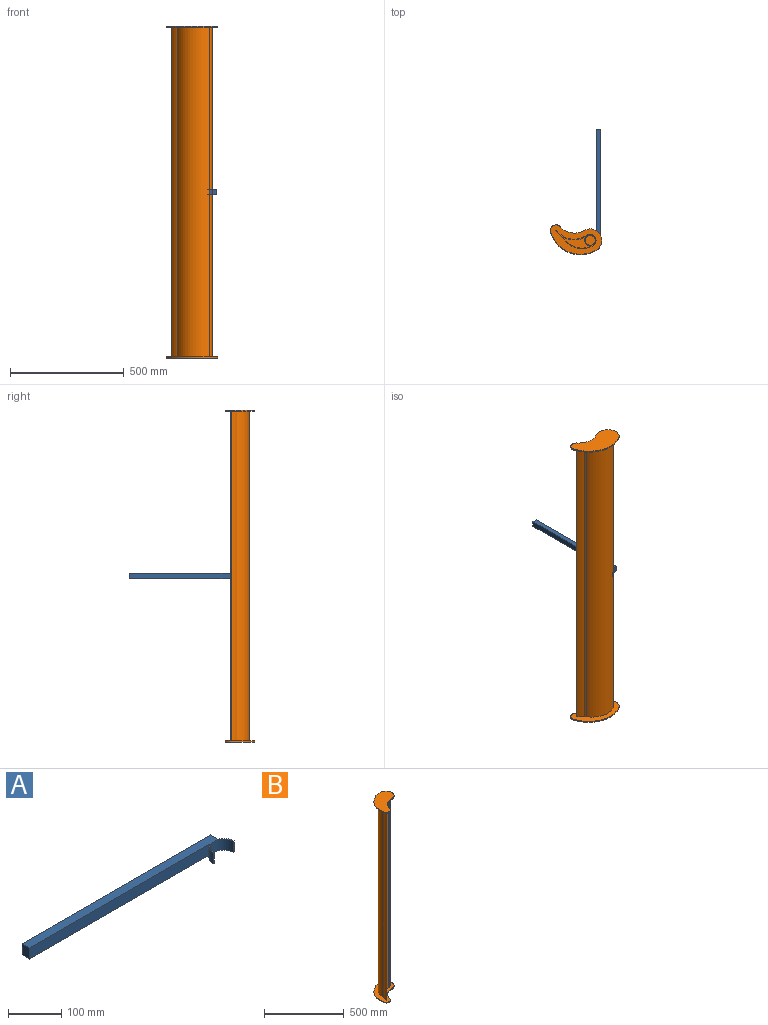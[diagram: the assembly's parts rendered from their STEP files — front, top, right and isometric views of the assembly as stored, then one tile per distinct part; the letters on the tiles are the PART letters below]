
ASSEMBLY  parts=2 mates=1
PART A: 11 faces, bbox 517.5x45x25 mm
  f0: plane 25x20mm, normal (-1,0,0), area 500mm2, adj f1,f8,f9,f10
  f1: plane 478.54x25mm, normal (0,-1,0), area 11963.6mm2, adj f0,f2,f9,f10
  f2: cylinder r=27.5mm len=25mm, axis (0,0,-1), area 784.5mm2, adj f1,f3,f9,f10
  f3: plane 25x2.5mm, normal (0,-1,0), area 62.5mm2, adj f2,f4,f9,f10
  f4: cylinder r=25mm len=50mm, axis (0,0,-1), area 1963.5mm2, adj f3,f5,f9,f10
  f5: plane 25x2.5mm, normal (0,-1,0), area 62.5mm2, adj f4,f6,f9,f10
  f6: cylinder r=27.5mm len=25.62mm, axis (0,0,-1), area 824.1mm2, adj f5,f7,f9,f10
  f7: plane 25x19.38mm, normal (1,0,0), area 484.6mm2, adj f6,f8,f9,f10
  f8: plane 500x25mm, normal (0,1,0), area 12500mm2, adj f0,f7,f9,f10
  f9: plane 517.5x45mm, normal (0,0,1), area 10168.1mm2, adj f0,f1,f2,f3,f4,f5,f6,f7
  f10: plane 517.5x45mm, normal (0,0,-1), area 10168.1mm2, adj f0,f1,f2,f3,f4,f5,f6,f7
PART B: 27 faces, bbox 186.8x187.7x1460 mm
  f0: cylinder r=25mm len=1450mm, axis (0,0,-1), area 113939.2mm2, adj f1,f6,f12,f18
  f1: plane 1450x2.5mm, normal (1,0,0), area 3625mm2, adj f0,f2,f12,f18
  f2: cylinder r=100mm len=1450mm, axis (0,0,-1), area 234624.9mm2, adj f1,f3,f12,f18
  f3: cylinder r=100mm len=1450mm, axis (0,0,-1), area 53859.5mm2, adj f2,f4,f12,f18
  f4: plane 1450x2.98mm, normal (-0.11,-0.99,0), area 4350mm2, adj f3,f5,f12,f18
  f5: cylinder r=97mm len=1450mm, axis (0,0,-1), area 220932.5mm2, adj f4,f6,f12,f18
  f6: plane 1450x2.64mm, normal (0.99,-0.11,0), area 3858.8mm2, adj f0,f5,f12,f18
  f7: cylinder r=88.03mm len=84.35mm, axis (0,0,-1), area 563.7mm2, adj f8,f10,f11,f12
  f8: cylinder r=50mm len=100mm, axis (0,0,-1), area 785.4mm2, adj f7,f9,f11,f12
  f9: cylinder r=136.78mm len=162.5mm, axis (0,0,-1), area 1203.7mm2, adj f8,f10,f11,f12
  f10: cylinder r=25mm len=50mm, axis (0,0,-1), area 392.7mm2, adj f7,f9,f11,f12
  f11: plane 187.67x186.79mm, normal (0,0,1), area 19238.2mm2, adj f7,f8,f9,f10
  f12: plane 187.67x186.79mm, normal (0,0,-1), area 13428.7mm2, adj f0,f1,f2,f3,f4,f5,f6,f7
  f13: cylinder r=88.03mm len=84.35mm, axis (0,0,1), area 563.7mm2, adj f14,f16,f17,f18
  f14: cylinder r=25mm len=50mm, axis (0,0,1), area 391mm2, adj f13,f15,f17,f18
  f15: cylinder r=136.84mm len=162.85mm, axis (0,0,1), area 1205.6mm2, adj f14,f16,f17,f18
  f16: cylinder r=50mm len=100mm, axis (0,0,1), area 785.4mm2, adj f13,f15,f17,f18
  f17: plane 187.67x186.84mm, normal (0,0,-1), area 19244.1mm2, adj f13,f14,f15,f16
  f18: plane 187.67x186.84mm, normal (0,0,1), area 13434.5mm2, adj f0,f1,f2,f3,f4,f5,f6,f13
  f19: plane 96.47x91.25mm, normal (0,0,-1), area 2915.5mm2, adj f20,f21,f22
  f20: cylinder r=25mm len=1450mm, axis (0,0,-1), area 95829.6mm2, adj f19,f21,f22,f23
  f21: cylinder r=100mm len=1450mm, axis (0,0,-1), area 155856.6mm2, adj f19,f20,f22,f23
  f22: cylinder r=97mm len=1450mm, axis (0,0,-1), area 212059.6mm2, adj f19,f20,f21,f23
  f23: plane 96.47x91.25mm, normal (0,0,1), area 2915.5mm2, adj f20,f21,f22
  f24: plane 44x44mm, normal (0,0,1), area 1520.5mm2, adj f26
  f25: plane 44x44mm, normal (0,0,-1), area 1520.5mm2, adj f26
  f26: cylinder r=22mm len=1450mm, axis (0,0,-1), area 200433.6mm2, adj f24,f25
PLACE A rot(axis=(0,0,-1),90deg) t=(-10,0,-12.5)mm
PLACE B rot(axis=(0.97,0.26,0),180deg) t=(-35,-490,725)mm
MATE revolute B.f0 <-> A.f2  axis (0,0,1) through (-35,-490,0)mm
